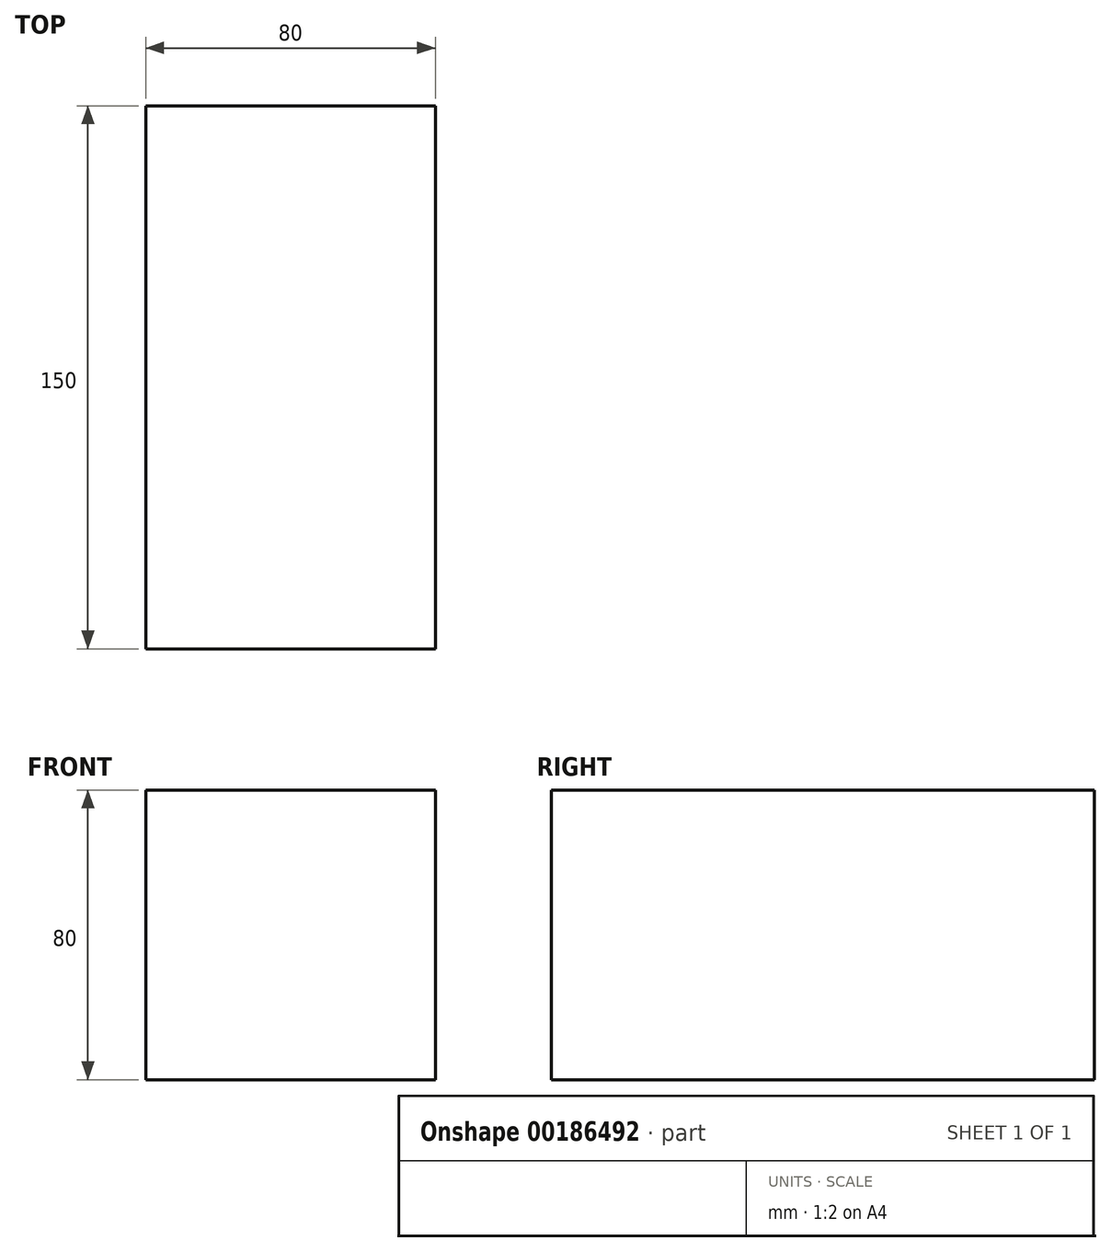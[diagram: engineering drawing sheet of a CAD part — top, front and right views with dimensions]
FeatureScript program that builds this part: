
annotation { "Feature Type Name" : "Feature", "Feature Type Description" : "" }
export const myFeature = defineFeature(function(context is Context, id is Id, definition is map)
    precondition{}
    {
        {
            var Q0;
            Q0=qCreatedBy(makeId("Front.planeOp"),FACE);
            var sketch = newSketch(context, id + "F0", { "sketchPlane" : qUnion([Q0])});
            skLineSegment(sketch, "E0.bottom", {"start": v(40, 0) * mm, "end": v(-40, 0) * mm});
            skLineSegment(sketch, "E0.top", {"start": v(40, 80) * mm, "end": v(-40, 80) * mm});
            skLineSegment(sketch, "E0.left", {"start": v(40, 0) * mm, "end": v(40, 80) * mm});
            skLineSegment(sketch, "E0.right", {"start": v(-40, 0) * mm, "end": v(-40, 80) * mm});
            skPoint(sketch, "E0.middle", {"position": v(0, 40) * mm});
            skSolve(sketch);
        }
        {
            var Q0;
            Q0 = qSketchRegion(id + "F0", true);
            extrude(context, id + "F1", {"entities" : qUnion([Q0]), "depth" : 150 * mm});
        }
    });
